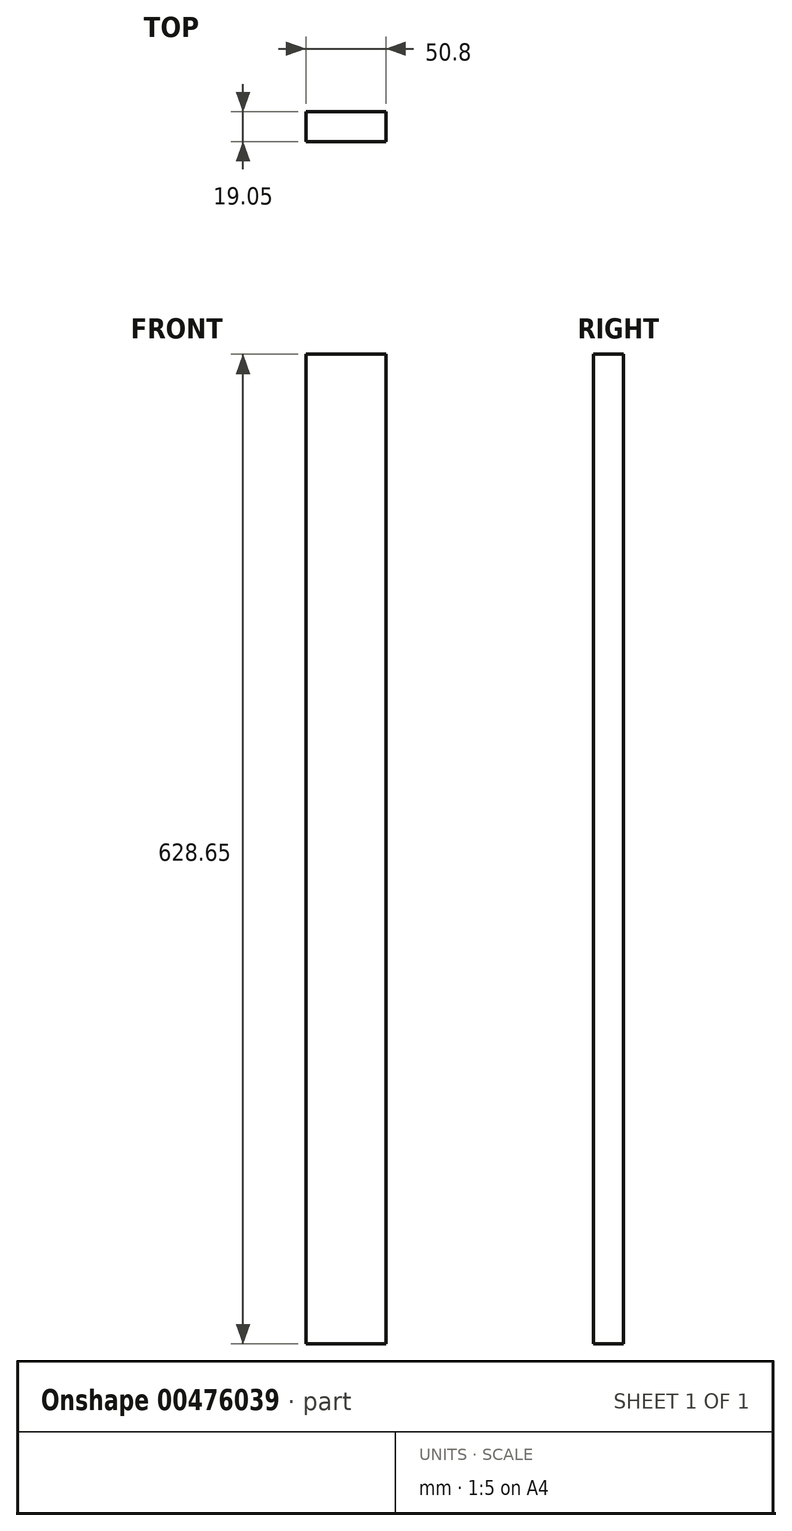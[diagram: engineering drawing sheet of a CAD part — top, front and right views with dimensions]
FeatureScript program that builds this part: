
annotation { "Feature Type Name" : "Feature", "Feature Type Description" : "" }
export const myFeature = defineFeature(function(context is Context, id is Id, definition is map)
    precondition{}
    {
        {
            var Q0;
            Q0=qCreatedBy(makeId("Front.planeOp"),FACE);
            var sketch = newSketch(context, id + "F0", { "sketchPlane" : qUnion([Q0])});
            skLineSegment(sketch, "E0.bottom", {"start": v(0, 0) * mm, "end": v(50.8, 0) * mm});
            skLineSegment(sketch, "E0.top", {"start": v(0, 628.65) * mm, "end": v(50.8, 628.65) * mm});
            skLineSegment(sketch, "E0.left", {"start": v(0, 0) * mm, "end": v(0, 628.65) * mm});
            skLineSegment(sketch, "E0.right", {"start": v(50.8, 0) * mm, "end": v(50.8, 628.65) * mm});
            skSolve(sketch);
        }
        {
            var Q0;
            Q0 = qSketchRegion(id + "F0", true);
            extrude(context, id + "F1", {"entities" : qUnion([Q0]), "depth" : 19.05 * mm});
        }
    });
